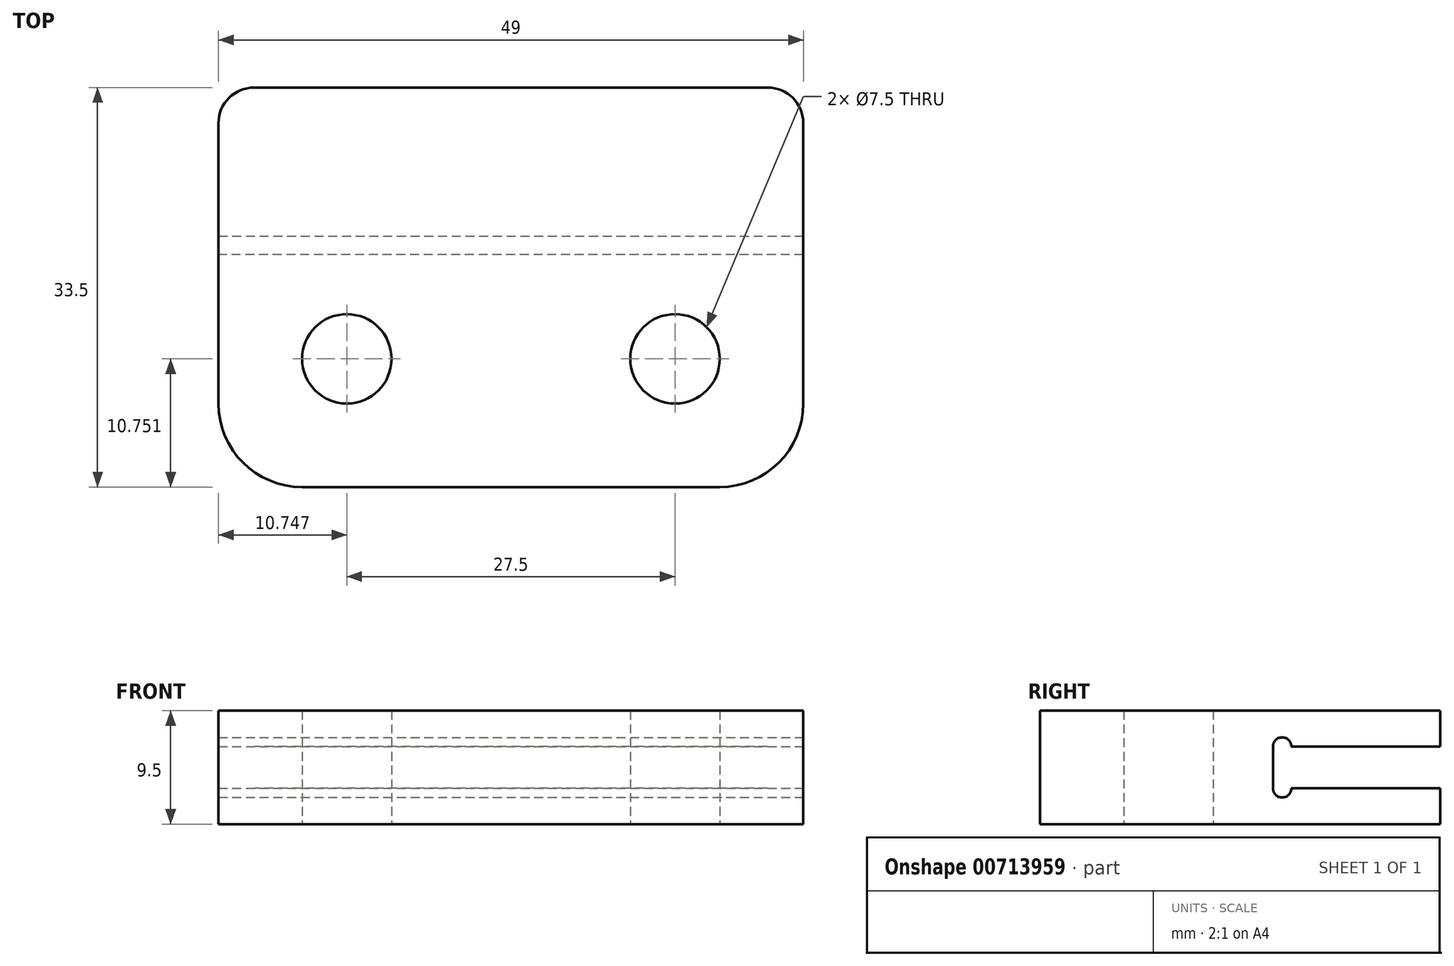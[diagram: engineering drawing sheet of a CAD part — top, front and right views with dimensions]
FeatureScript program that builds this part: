
annotation { "Feature Type Name" : "Feature", "Feature Type Description" : "" }
export const myFeature = defineFeature(function(context is Context, id is Id, definition is map)
    precondition{}
    {
        {
            var Q0;
            Q0=qCreatedBy(makeId("Top.planeOp"),FACE);
            var sketch = newSketch(context, id + "F0", { "sketchPlane" : qUnion([Q0])});
            skLineSegment(sketch, "E0.bottom", {"start": v(-21.27, -13.47) * mm, "end": v(27.73, -13.47) * mm});
            skLineSegment(sketch, "E0.top", {"start": v(-21.27, 20.03) * mm, "end": v(27.73, 20.03) * mm});
            skLineSegment(sketch, "E0.left", {"start": v(-21.27, -13.47) * mm, "end": v(-21.27, 20.03) * mm});
            skLineSegment(sketch, "E0.right", {"start": v(27.73, -13.47) * mm, "end": v(27.73, 20.03) * mm});
            skPoint(sketch, "E1", {"position": v(-10.52, -2.72) * mm});
            skPoint(sketch, "E2", {"position": v(16.98, -2.72) * mm});
            skCircle(sketch, "E3", {"center": v(-10.52, -2.72) * mm, "radius": 3.75 * mm});
            skCircle(sketch, "E4", {"center": v(16.98, -2.72) * mm, "radius": 3.75 * mm});
            skSolve(sketch);
        }
        {
            var Q0;
            Q0=makeQuery(id+"F0.imprint","IMPRINT",FACE,{"disambiguationData":[TD([[makeQuery(id+"F0.imprint","IMPRINT",EDGE,{"derivedFrom":sQuery(id+"F0.wireOp",EDGE,"E0.bottom")}),1.0]])]});
            extrude(context, id + "F1", {"entities" : qUnion([Q0]), "depth" : 9.5 * mm, "offsetDistance" : 25 * mm});
        }
        {
            var Q0;
            Q0=makeQuery(id+"F1.opExtrude","SWEPT_EDGE",EDGE,{"disambiguationData":[OSD([sQuery(id+"F0.wireOp",EDGE,"E0.bottom"),sQuery(id+"F0.wireOp",EDGE,"E0.left")])]});
            var Q1;
            Q1=makeQuery(id+"F1.opExtrude","SWEPT_EDGE",EDGE,{"disambiguationData":[OSD([sQuery(id+"F0.wireOp",EDGE,"E0.bottom"),sQuery(id+"F0.wireOp",EDGE,"E0.right")])]});
            fillet(context, id + "F2", {"entities" : qUnion([Q0, Q1]), "radius" : 7 * mm, "tangentPropagation" : true, "allowEdgeOverflow" : false});
        }
        {
            var Q0;
            Q0=makeQuery(id+"F1.opExtrude","SWEPT_FACE",FACE,{"disambiguationData":[OSD([sQuery(id+"F0.wireOp",EDGE,"E0.top")])]});
            var sketch = newSketch(context, id + "F3", { "sketchPlane" : qUnion([Q0])});
            skLineSegment(sketch, "E5.bottom", {"start": v(-27.73, 3) * mm, "end": v(21.27, 3) * mm});
            skLineSegment(sketch, "E5.top", {"start": v(-27.73, 6.5) * mm, "end": v(21.27, 6.5) * mm});
            skLineSegment(sketch, "E5.left", {"start": v(-27.73, 3) * mm, "end": v(-27.73, 6.5) * mm});
            skLineSegment(sketch, "E5.right", {"start": v(21.27, 3) * mm, "end": v(21.27, 6.5) * mm});
            skPoint(sketch, "E5.middle", {"position": v(-3.23, 4.75) * mm});
            skPoint(sketch, "E5.middle.positionSnap0", {"position": v(-3.23, 9.5) * mm});
            skPoint(sketch, "E5.middle.positionSnap1", {"position": v(21.27, 4.75) * mm});
            skPoint(sketch, "E5.centerSnap0", {"position": v(-3.23, 9.5) * mm});
            skPoint(sketch, "E5.centerSnap1", {"position": v(21.27, 4.75) * mm});
            skSolve(sketch);
        }
        {
            var Q0;
            Q0=makeQuery(id+"F1.opExtrude","SWEPT_EDGE",EDGE,{"disambiguationData":[OSD([sQuery(id+"F0.wireOp",EDGE,"E0.top"),sQuery(id+"F0.wireOp",EDGE,"E0.right")])]});
            var Q1;
            Q1=makeQuery(id+"F1.opExtrude","SWEPT_EDGE",EDGE,{"disambiguationData":[OSD([sQuery(id+"F0.wireOp",EDGE,"E0.top"),sQuery(id+"F0.wireOp",EDGE,"E0.left")])]});
            fillet(context, id + "F4", {"entities" : qUnion([Q0, Q1]), "radius" : 3 * mm, "tangentPropagation" : true, "allowEdgeOverflow" : false});
        }
        {
            var Q0;
            Q0=makeQuery(id+"F3.imprint","IMPRINT",FACE,{"disambiguationData":[TD([[makeQuery(id+"F3.imprint","IMPRINT",EDGE,{"derivedFrom":sQuery(id+"F3.wireOp",EDGE,"E5.bottom")}),1.0]])]});
            extrude(context, id + "F5", {"entities" : qUnion([Q0]), "operationType" : NewBodyOperationType.REMOVE, "oppositeDirection" : true, "depth" : 14 * mm, "offsetDistance" : 25 * mm});
        }
        {
            var Q0;
            Q0=makeQuery(id+"F1.opExtrude","SWEPT_FACE",FACE,{"disambiguationData":[OSD([sQuery(id+"F0.wireOp",EDGE,"E0.right")])]});
            var sketch = newSketch(context, id + "F6", { "sketchPlane" : qUnion([Q0])});
            skLineSegment(sketch, "E6.bottom", {"start": v(6.03, 6.5) * mm, "end": v(7.58, 6.5) * mm});
            skLineSegment(sketch, "E6.top", {"start": v(6.03, 3) * mm, "end": v(7.58, 3) * mm});
            skLineSegment(sketch, "E6.left", {"start": v(6.03, 6.5) * mm, "end": v(6.03, 3) * mm});
            skLineSegment(sketch, "E6.right", {"start": v(7.58, 6.5) * mm, "end": v(7.58, 3) * mm});
            skCircle(sketch, "E7", {"center": v(6.8, 6.5) * mm, "radius": 0.77 * mm});
            skCircle(sketch, "E8", {"center": v(6.8, 3) * mm, "radius": 0.77 * mm});
            skSolve(sketch);
        }
        {
            var Q0;
            {var subQ0=sQuery(id+"F6.wireOp",EDGE,"E6.bottom");Q0=makeQuery(id+"F6.imprint","IMPRINT",FACE,{"disambiguationData":[TD([[makeQuery(id+"F6.imprint","IMPRINT",EDGE,{"derivedFrom":subQ0}),1.0]])]});}
            var Q1;
            {var subQ0=sQuery(id+"F6.wireOp",EDGE,"E6.top");Q1=makeQuery(id+"F6.imprint","IMPRINT",FACE,{"disambiguationData":[TD([[makeQuery(id+"F6.imprint","IMPRINT",EDGE,{"derivedFrom":subQ0}),-1.0]])]});}
            extrude(context, id + "F7", {"entities" : qUnion([Q0, Q1]), "operationType" : NewBodyOperationType.REMOVE, "oppositeDirection" : true, "depth" : 50 * mm, "offsetDistance" : 25 * mm});
        }
    });
